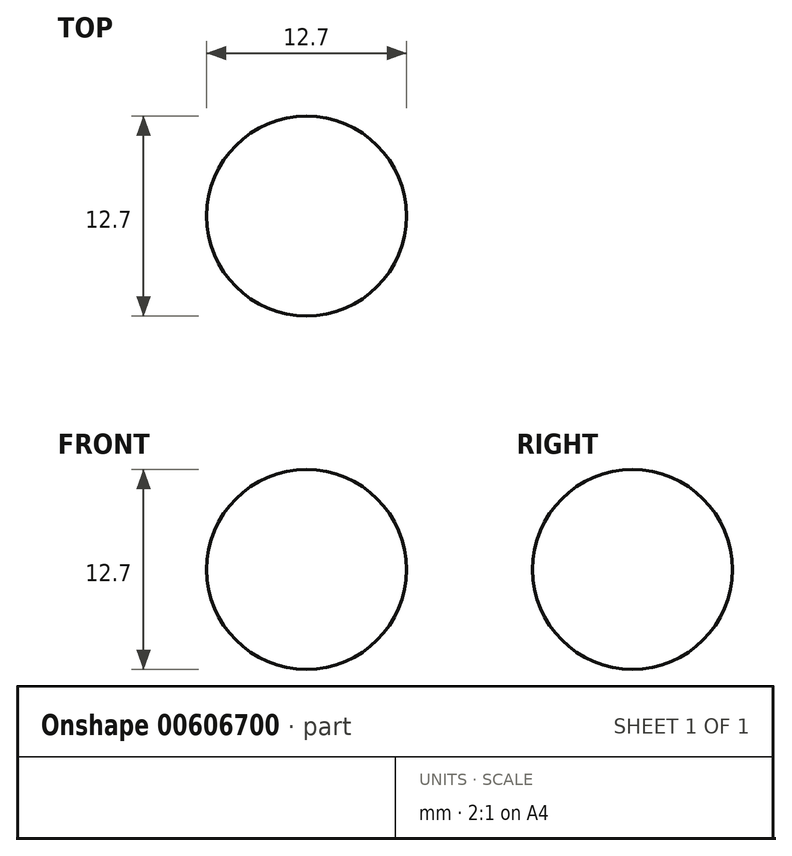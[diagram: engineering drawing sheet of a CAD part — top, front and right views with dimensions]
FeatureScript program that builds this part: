
annotation { "Feature Type Name" : "Feature", "Feature Type Description" : "" }
export const myFeature = defineFeature(function(context is Context, id is Id, definition is map)
    precondition{}
    {
        {
            var Q0;
            Q0=qCreatedBy(makeId("Top.planeOp"),FACE);
            var sketch = newSketch(context, id + "F0", { "sketchPlane" : qUnion([Q0])});
            skCircle(sketch, "E0", {"center": v(0, 0) * mm, "radius": 6.35 * mm});
            skLineSegment(sketch, "E1", {"start": v(0, 6.35) * mm, "end": v(0, -6.35) * mm});
            skSolve(sketch);
        }
        {
            var Q0;
            {var subQ0=sQuery(id+"F0.wireOp",EDGE,"E1");Q0=makeQuery(id+"F0.imprint","IMPRINT",FACE,{"disambiguationData":[TD([[makeQuery(id+"F0.imprint","IMPRINT",EDGE,{"derivedFrom":subQ0}),-1.0]])]});}
            var Q1;
            Q1=sQuery(id+"F0.wireOp",EDGE,"E1");
            revolve(context, id + "F1", {"entities" : qUnion([Q0]), "axis" : qUnion([Q1]), "revolveType" : RevolveType.FULL});
        }
    });
